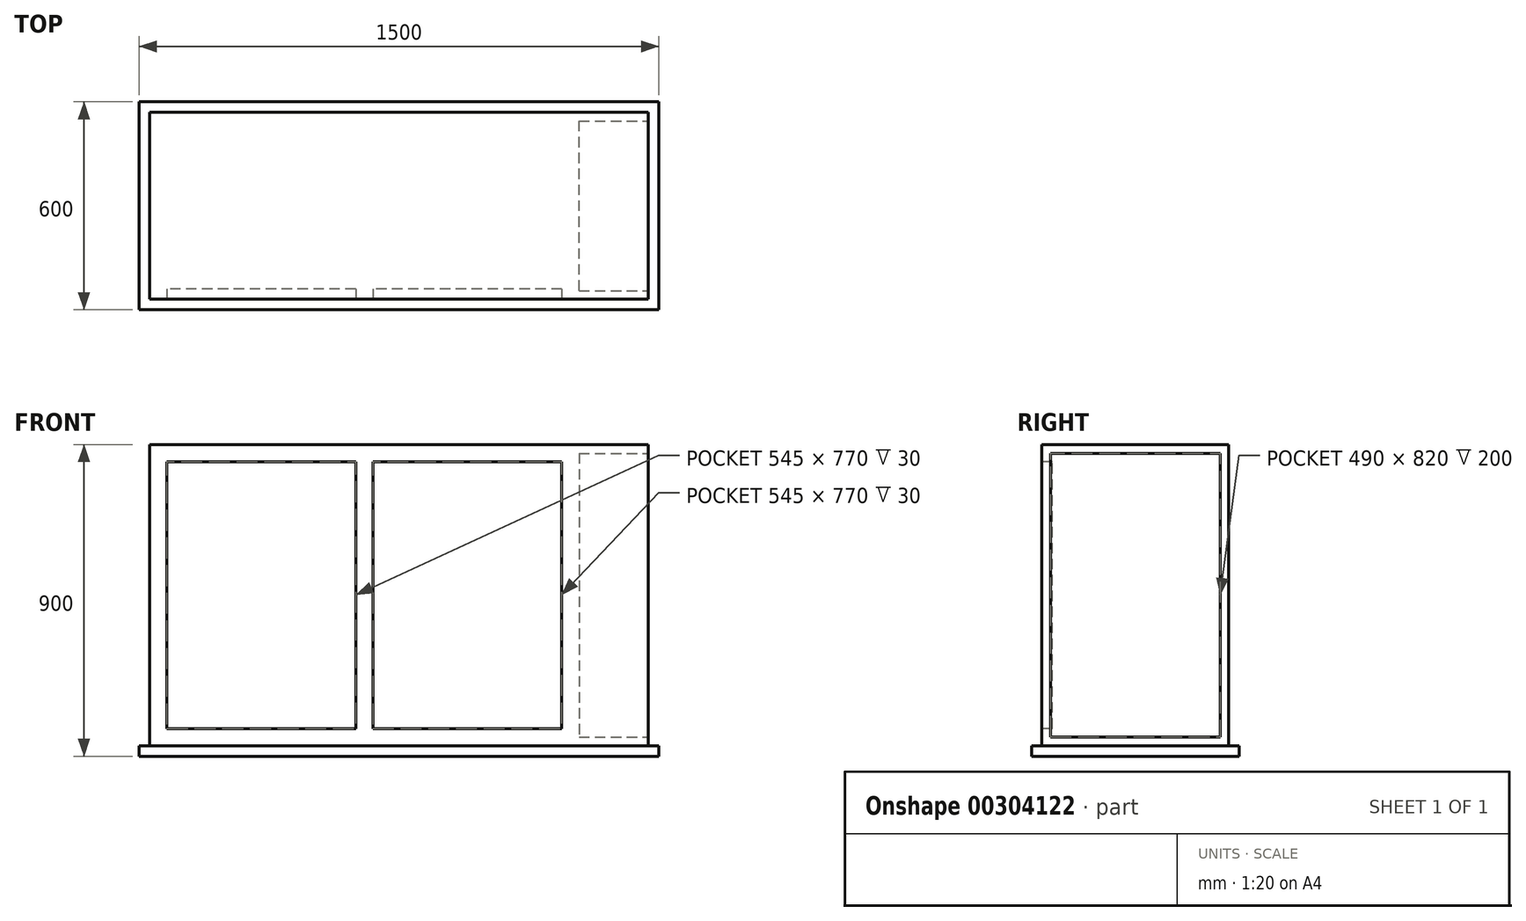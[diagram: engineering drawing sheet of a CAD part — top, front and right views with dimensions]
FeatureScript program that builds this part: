
annotation { "Feature Type Name" : "Feature", "Feature Type Description" : "" }
export const myFeature = defineFeature(function(context is Context, id is Id, definition is map)
    precondition{}
    {
        {
            var Q0;
            Q0=qCreatedBy(makeId("Top.planeOp"),FACE);
            var sketch = newSketch(context, id + "F0", { "sketchPlane" : qUnion([Q0])});
            skLineSegment(sketch, "E0.bottom", {"start": v(-901.4, 54.33) * mm, "end": v(598.6, 54.33) * mm});
            skLineSegment(sketch, "E0.top", {"start": v(-901.4, -545.67) * mm, "end": v(598.6, -545.67) * mm});
            skLineSegment(sketch, "E0.left", {"start": v(-901.4, 54.33) * mm, "end": v(-901.4, -545.67) * mm});
            skLineSegment(sketch, "E0.right", {"start": v(598.6, 54.33) * mm, "end": v(598.6, -545.67) * mm});
            skSolve(sketch);
        }
        {
            var Q0;
            Q0=makeQuery(id+"F0.imprint","IMPRINT",FACE,{"disambiguationData":[TD([[makeQuery(id+"F0.imprint","IMPRINT",EDGE,{"derivedFrom":sQuery(id+"F0.wireOp",EDGE,"E0.bottom")}),-1.0]])]});
            extrude(context, id + "F1", {"entities" : qUnion([Q0]), "depth" : 30 * mm, "offsetDistance" : 25 * mm});
        }
        {
            var Q0;
            Q0=makeQuery(id+"F1.opExtrude","CAP_FACE",FACE,{"disambiguationData":[OSD([sQuery(id+"F0.wireOp",EDGE,"E0.bottom"),sQuery(id+"F0.wireOp",EDGE,"E0.top"),sQuery(id+"F0.wireOp",EDGE,"E0.left"),sQuery(id+"F0.wireOp",EDGE,"E0.right")])],"isStart":false});
            var sketch = newSketch(context, id + "F2", { "sketchPlane" : qUnion([Q0])});
            skLineSegment(sketch, "E1.0", {"start": v(-871.4, 24.33) * mm, "end": v(-871.4, -515.67) * mm});
            skLineSegment(sketch, "E1.1", {"start": v(568.6, 24.33) * mm, "end": v(-871.4, 24.33) * mm});
            skLineSegment(sketch, "E1.2", {"start": v(568.6, -515.67) * mm, "end": v(568.6, 24.33) * mm});
            skLineSegment(sketch, "E1.3", {"start": v(-871.4, -515.67) * mm, "end": v(568.6, -515.67) * mm});
            skSolve(sketch);
        }
        {
            var Q0;
            Q0=makeQuery(id+"F2.imprint","IMPRINT",FACE,{"disambiguationData":[TD([[makeQuery(id+"F2.imprint","IMPRINT",EDGE,{"derivedFrom":sQuery(id+"F2.wireOp",EDGE,"E1.0")}),1.0]])]});
            extrude(context, id + "F3", {"entities" : qUnion([Q0]), "depth" : 870 * mm, "offsetDistance" : 25 * mm});
        }
        {
            var Q0;
            Q0=makeQuery(id+"F3.opExtrude","SWEPT_FACE",FACE,{"disambiguationData":[OSD([sQuery(id+"F2.wireOp",EDGE,"E1.2")])]});
            var sketch = newSketch(context, id + "F4", { "sketchPlane" : qUnion([Q0])});
            skLineSegment(sketch, "E2.0", {"start": v(-490.67, 55) * mm, "end": v(-0.67, 55) * mm});
            skLineSegment(sketch, "E2.1", {"start": v(-490.67, 875) * mm, "end": v(-490.67, 55) * mm});
            skLineSegment(sketch, "E2.2", {"start": v(-0.67, 875) * mm, "end": v(-490.67, 875) * mm});
            skLineSegment(sketch, "E2.3", {"start": v(-0.67, 55) * mm, "end": v(-0.67, 875) * mm});
            skSolve(sketch);
        }
        {
            var Q0;
            Q0=makeQuery(id+"F4.imprint","IMPRINT",FACE,{"disambiguationData":[TD([[makeQuery(id+"F4.imprint","IMPRINT",EDGE,{"derivedFrom":sQuery(id+"F4.wireOp",EDGE,"E2.0")}),1.0]])]});
            extrude(context, id + "F5", {"entities" : qUnion([Q0]), "operationType" : NewBodyOperationType.REMOVE, "oppositeDirection" : true, "depth" : 200 * mm, "offsetDistance" : 25 * mm});
        }
        {
            var Q0;
            Q0=makeQuery(id+"F3.opExtrude","SWEPT_FACE",FACE,{"disambiguationData":[OSD([sQuery(id+"F2.wireOp",EDGE,"E1.3")])]});
            var sketch = newSketch(context, id + "F6", { "sketchPlane" : qUnion([Q0])});
            skLineSegment(sketch, "E3.bottom", {"start": v(318.6, 80) * mm, "end": v(-226.4, 80) * mm});
            skLineSegment(sketch, "E3.top", {"start": v(318.6, 850) * mm, "end": v(-226.4, 850) * mm});
            skLineSegment(sketch, "E3.left", {"start": v(318.6, 80) * mm, "end": v(318.6, 850) * mm});
            skLineSegment(sketch, "E3.right", {"start": v(-226.4, 80) * mm, "end": v(-226.4, 850) * mm});
            skLineSegment(sketch, "E4.bottom", {"start": v(-276.4, 80) * mm, "end": v(-821.4, 80) * mm});
            skLineSegment(sketch, "E4.top", {"start": v(-276.4, 850) * mm, "end": v(-821.4, 850) * mm});
            skLineSegment(sketch, "E4.left", {"start": v(-276.4, 80) * mm, "end": v(-276.4, 850) * mm});
            skLineSegment(sketch, "E4.right", {"start": v(-821.4, 80) * mm, "end": v(-821.4, 850) * mm});
            skSolve(sketch);
        }
        {
            var Q0;
            Q0=makeQuery(id+"F6.imprint","IMPRINT",FACE,{"disambiguationData":[TD([[makeQuery(id+"F6.imprint","IMPRINT",EDGE,{"derivedFrom":sQuery(id+"F6.wireOp",EDGE,"E3.bottom")}),-1.0]])]});
            var Q1;
            Q1=makeQuery(id+"F6.imprint","IMPRINT",FACE,{"disambiguationData":[TD([[makeQuery(id+"F6.imprint","IMPRINT",EDGE,{"derivedFrom":sQuery(id+"F6.wireOp",EDGE,"E4.bottom")}),-1.0]])]});
            extrude(context, id + "F7", {"entities" : qUnion([Q0, Q1]), "operationType" : NewBodyOperationType.REMOVE, "oppositeDirection" : true, "depth" : 30 * mm, "offsetDistance" : 25 * mm});
        }
    });
